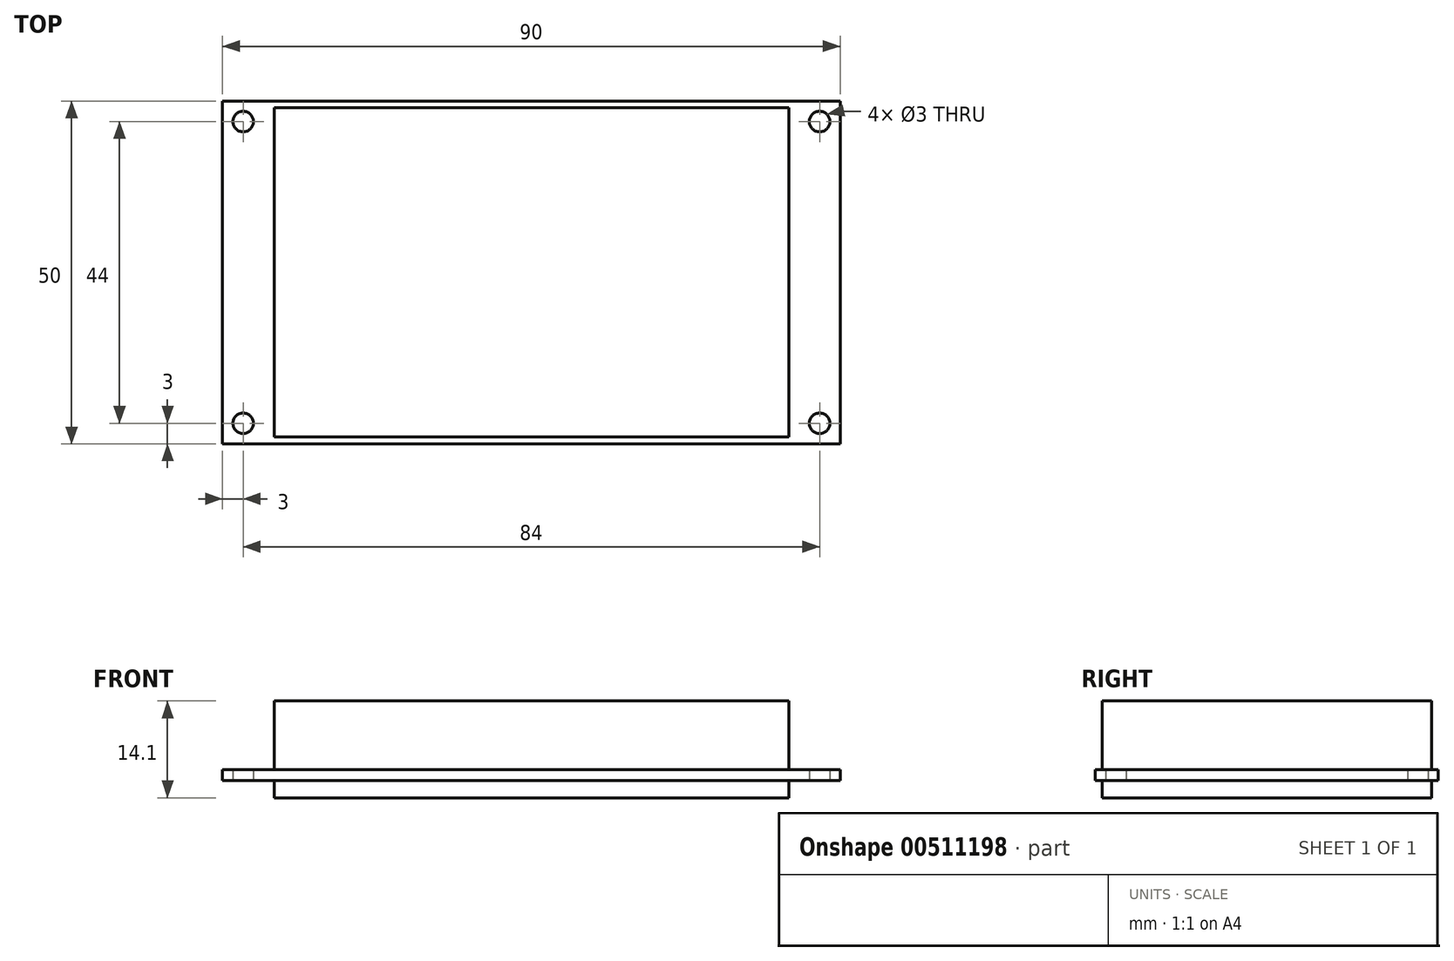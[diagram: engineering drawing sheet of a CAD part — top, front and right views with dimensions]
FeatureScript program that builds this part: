
annotation { "Feature Type Name" : "Feature", "Feature Type Description" : "" }
export const myFeature = defineFeature(function(context is Context, id is Id, definition is map)
    precondition{}
    {
        {
            var Q0;
            Q0=qCreatedBy(makeId("Top.planeOp"),FACE);
            var sketch = newSketch(context, id + "F0", { "sketchPlane" : qUnion([Q0])});
            skLineSegment(sketch, "E0.bottom", {"start": v(45, -25) * mm, "end": v(-45, -25) * mm});
            skLineSegment(sketch, "E0.top", {"start": v(45, 25) * mm, "end": v(-45, 25) * mm});
            skLineSegment(sketch, "E0.left", {"start": v(45, -25) * mm, "end": v(45, 25) * mm});
            skLineSegment(sketch, "E0.right", {"start": v(-45, -25) * mm, "end": v(-45, 25) * mm});
            skPoint(sketch, "E0.middle", {"position": v(0, 0) * mm});
            skCircle(sketch, "E1", {"center": v(-42, -22) * mm, "radius": 1.5 * mm});
            skCircle(sketch, "E2.MirrorC", {"center": v(42, -22) * mm, "radius": 1.5 * mm});
            skCircle(sketch, "E3.MirrorC", {"center": v(-42, 22) * mm, "radius": 1.5 * mm});
            skCircle(sketch, "E4.MirrorC", {"center": v(42, 22) * mm, "radius": 1.5 * mm});
            skLineSegment(sketch, "E5.bottom", {"start": v(37.5, -24) * mm, "end": v(-37.5, -24) * mm});
            skLineSegment(sketch, "E5.top", {"start": v(37.5, 24) * mm, "end": v(-37.5, 24) * mm});
            skLineSegment(sketch, "E5.left", {"start": v(37.5, -24) * mm, "end": v(37.5, 24) * mm});
            skLineSegment(sketch, "E5.right", {"start": v(-37.5, -24) * mm, "end": v(-37.5, 24) * mm});
            skSolve(sketch);
        }
        {
            var Q0;
            Q0=makeQuery(id+"F0.imprint","IMPRINT",FACE,{"disambiguationData":[TD([[makeQuery(id+"F0.imprint","IMPRINT",EDGE,{"derivedFrom":sQuery(id+"F0.wireOp",EDGE,"E0.bottom")}),-1.0]])]});
            var Q1;
            Q1=makeQuery(id+"F0.imprint","IMPRINT",FACE,{"disambiguationData":[TD([[makeQuery(id+"F0.imprint","IMPRINT",EDGE,{"derivedFrom":sQuery(id+"F0.wireOp",EDGE,"E5.bottom")}),-1.0]])]});
            extrude(context, id + "F1", {"entities" : qUnion([Q0, Q1]), "depth" : 1.6 * mm});
        }
        {
            var Q0;
            Q0=makeQuery(id+"F1.opExtrude","CAP_FACE",FACE,{"disambiguationData":[OSD([sQuery(id+"F0.wireOp",EDGE,"E0.bottom"),sQuery(id+"F0.wireOp",EDGE,"E0.top"),sQuery(id+"F0.wireOp",EDGE,"E0.left"),sQuery(id+"F0.wireOp",EDGE,"E0.right"),sQuery(id+"F0.wireOp",EDGE,"E1"),sQuery(id+"F0.wireOp",EDGE,"E2.MirrorC"),sQuery(id+"F0.wireOp",EDGE,"E3.MirrorC"),sQuery(id+"F0.wireOp",EDGE,"E4.MirrorC")])],"isStart":false});
            cPlane(context, id + "F2", {"entities" : qUnion([Q0]), "cplaneType" : CPlaneType.OFFSET, "offset" : 0 * mm, "width" : 150 * mm, "height" : 150 * mm});
        }
        {
            var Q0;
            Q0=qCreatedBy(id+"F2.planeOp",FACE);
            var sketch = newSketch(context, id + "F3", { "sketchPlane" : qUnion([Q0])});
            skLineSegment(sketch, "E6.bottom", {"start": v(37.5, -24) * mm, "end": v(-37.5, -24) * mm});
            skLineSegment(sketch, "E6.top", {"start": v(37.5, 24) * mm, "end": v(-37.5, 24) * mm});
            skLineSegment(sketch, "E6.left", {"start": v(37.5, -24) * mm, "end": v(37.5, 24) * mm});
            skLineSegment(sketch, "E6.right", {"start": v(-37.5, -24) * mm, "end": v(-37.5, 24) * mm});
            skPoint(sketch, "E6.middle", {"position": v(0, 0) * mm});
            skSolve(sketch);
        }
        {
            var Q0;
            Q0=makeQuery(id+"F3.imprint","IMPRINT",FACE,{"disambiguationData":[TD([[makeQuery(id+"F3.imprint","IMPRINT",EDGE,{"derivedFrom":sQuery(id+"F3.wireOp",EDGE,"E6.bottom")}),-1.0]])]});
            extrude(context, id + "F4", {"entities" : qUnion([Q0]), "depth" : 10 * mm});
        }
        {
            var Q0;
            Q0=makeQuery(id+"F0.imprint","IMPRINT",FACE,{"disambiguationData":[TD([[makeQuery(id+"F0.imprint","IMPRINT",EDGE,{"derivedFrom":sQuery(id+"F0.wireOp",EDGE,"E5.bottom")}),-1.0]])]});
            extrude(context, id + "F5", {"entities" : qUnion([Q0]), "oppositeDirection" : true, "depth" : 2.5 * mm});
        }
    });
